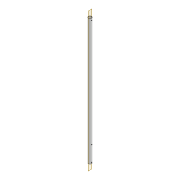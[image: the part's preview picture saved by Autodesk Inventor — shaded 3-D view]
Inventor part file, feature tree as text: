
AUTODESK INVENTOR PART (.ipt)
format: ipt  version: 2022 (Build 260153000, 153)  size: 107,520 bytes
history: native  units: mm
features: extrude x2, sketch x2
ambient origin geometry x8: Origin, YZ Plane, XZ Plane, XY Plane, X Axis, Y Axis, Z Axis, Center Point
bodies: Solid1 (feature_tree)
feature tree (4):
  extrude  "Extrusion1"  Depth=10.0mm
  extrude  "Extrusion2"  Depth=4.0mm
  sketch  "Sketch1"  dims[d0=12.0mm d1=10.0mm]
  sketch  "Sketch2"  dims[d2=450.0mm d3=0.0mm d4=3.0mm d5=3.0mm d6=4.0mm d8=320.0mm d9=0.0mm d10=3.0mm d11=6.5mm d12=55.0mm d13=0.872665mm d14=0.5mm d15=0.872665mm]
